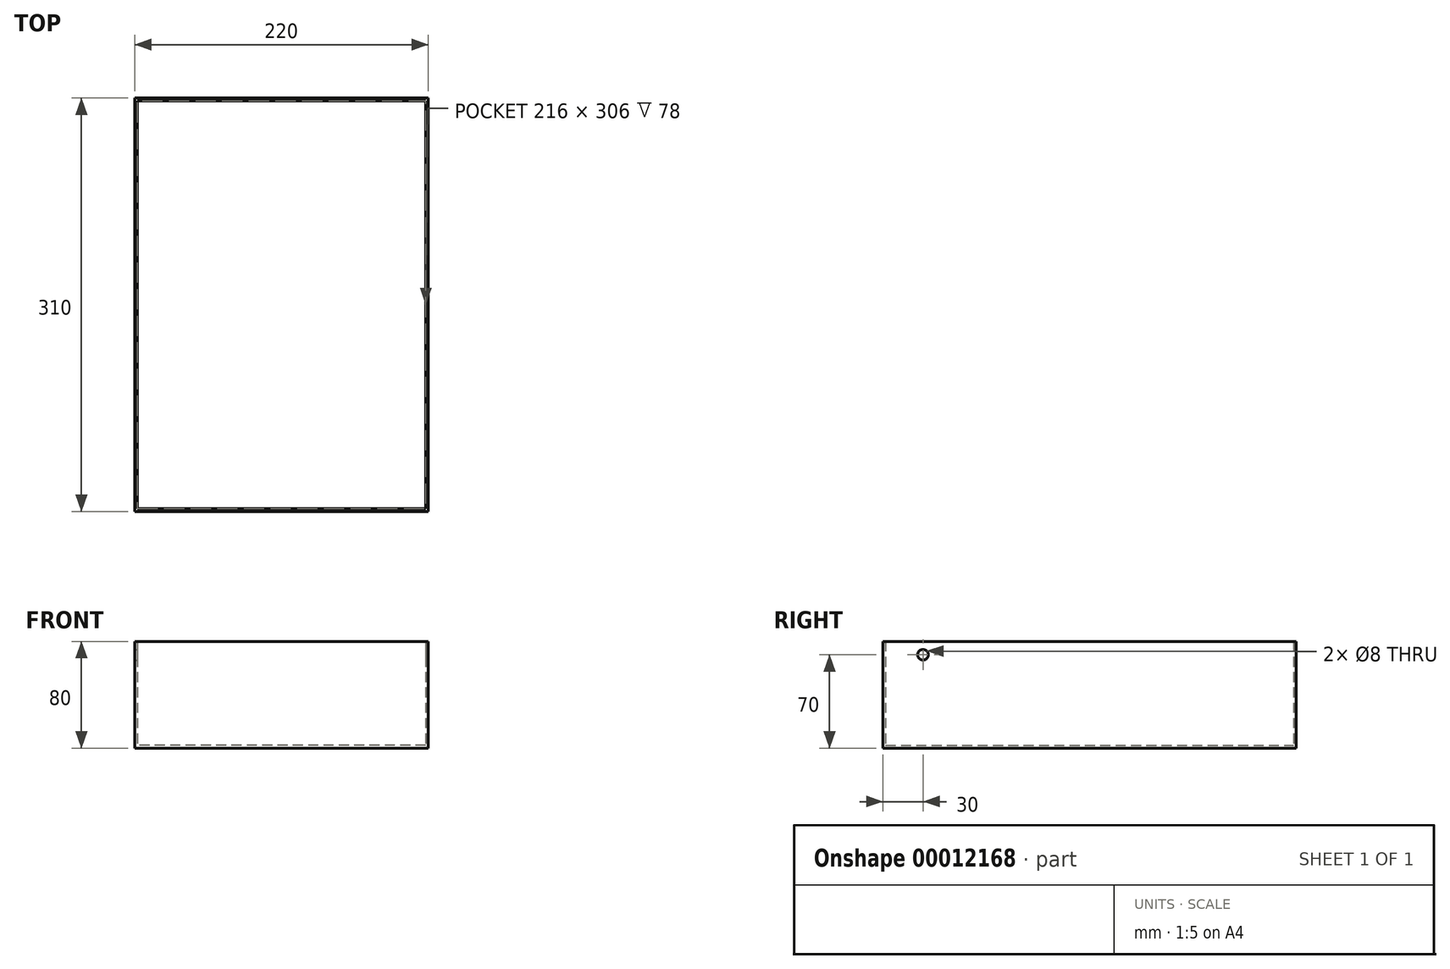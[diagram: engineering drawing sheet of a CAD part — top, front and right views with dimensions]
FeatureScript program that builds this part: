
annotation { "Feature Type Name" : "Feature", "Feature Type Description" : "" }
export const myFeature = defineFeature(function(context is Context, id is Id, definition is map)
    precondition{}
    {
        {
            var Q0;
            Q0=qCreatedBy(makeId("Top.planeOp"),FACE);
            var sketch = newSketch(context, id + "F0", { "sketchPlane" : qUnion([Q0])});
            skLineSegment(sketch, "E0.rect.bottom", {"start": v(110, -155) * mm, "end": v(-110, -155) * mm});
            skLineSegment(sketch, "E0.rect.top", {"start": v(110, 155) * mm, "end": v(-110, 155) * mm});
            skLineSegment(sketch, "E0.rect.left", {"start": v(110, -155) * mm, "end": v(110, 155) * mm});
            skLineSegment(sketch, "E0.rect.right", {"start": v(-110, -155) * mm, "end": v(-110, 155) * mm});
            skPoint(sketch, "E0.rect.middle", {"position": v(0, 0) * mm});
            skLineSegment(sketch, "E1.0", {"start": v(-108, -153) * mm, "end": v(-108, 153) * mm});
            skLineSegment(sketch, "E1.1", {"start": v(108, -153) * mm, "end": v(-108, -153) * mm});
            skLineSegment(sketch, "E1.2", {"start": v(108, -153) * mm, "end": v(108, 153) * mm});
            skLineSegment(sketch, "E1.3", {"start": v(108, 153) * mm, "end": v(-108, 153) * mm});
            skSolve(sketch);
        }
        {
            var Q0;
            Q0=makeQuery(id+"F0.imprint","IMPRINT",FACE,{"disambiguationData":[TD([[makeQuery(id+"F0.imprint","IMPRINT",EDGE,{"derivedFrom":sQuery(id+"F0.wireOp",EDGE,"E0.rect.bottom")}),-1.0]])]});
            extrude(context, id + "F1", {"entities" : qUnion([Q0]), "depth" : 80 * mm});
        }
        {
            var Q0;
            Q0=makeQuery(id+"F0.imprint","IMPRINT",FACE,{"disambiguationData":[TD([[makeQuery(id+"F0.imprint","IMPRINT",EDGE,{"derivedFrom":sQuery(id+"F0.wireOp",EDGE,"E1.0")}),-1.0]])]});
            extrude(context, id + "F2", {"entities" : qUnion([Q0]), "operationType" : NewBodyOperationType.ADD, "depth" : 2 * mm});
        }
        {
            var Q0;
            Q0=makeQuery(id+"F1.opExtrude","SWEPT_FACE",FACE,{"disambiguationData":[OSD([sQuery(id+"F0.wireOp",EDGE,"E0.rect.left")])]});
            var sketch = newSketch(context, id + "F3", { "sketchPlane" : qUnion([Q0])});
            skCircle(sketch, "E2", {"center": v(-125, 70) * mm, "radius": 4 * mm});
            skSolve(sketch);
        }
        {
            var Q0;
            Q0=makeQuery(id+"F3.imprint","IMPRINT",FACE,{"disambiguationData":[TD([[makeQuery(id+"F3.imprint","IMPRINT",EDGE,{"derivedFrom":sQuery(id+"F3.wireOp",EDGE,"E2")}),1.0]])]});
            extrude(context, id + "F4", {"entities" : qUnion([Q0]), "operationType" : NewBodyOperationType.REMOVE, "endBound" : BoundingType.THROUGH_ALL, "oppositeDirection" : true, "depth" : 25 * mm});
        }
    });
